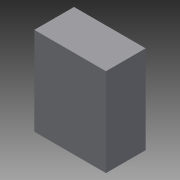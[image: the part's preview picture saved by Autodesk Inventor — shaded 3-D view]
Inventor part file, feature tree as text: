
AUTODESK INVENTOR PART (.ipt)
format: ipt  version: 2014 (Build 180170000, 170)  size: 99,328 bytes
history: native  units: mm
features: extrude x2, sketch x2
ambient origin geometry x8: Origin, YZ Plane, XZ Plane, XY Plane, X Axis, Y Axis, Z Axis, Center Point
bodies: Volumenkörper1 (feature_tree)
feature tree (4):
  extrude  "Extrusion1"  Depth=95.0mm
  extrude  "Extrusion2"  Depth=1.1mm
  sketch  "Skizze1"  dims[d0=70.0mm d1=95.0mm]
  sketch  "Skizze2"  dims[d2=1.0mm d3=0.0mm d4=1.1mm d5=40.0mm d6=0.0mm]
